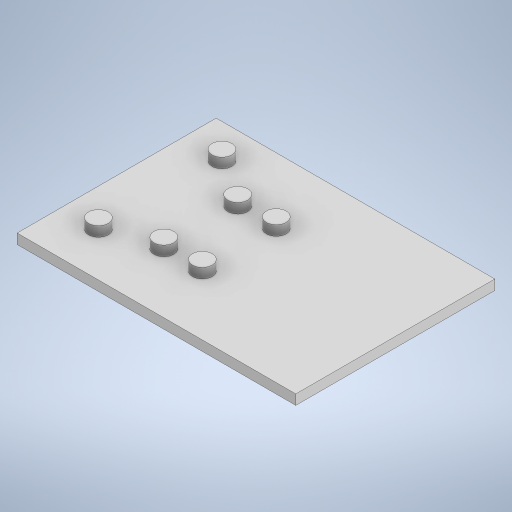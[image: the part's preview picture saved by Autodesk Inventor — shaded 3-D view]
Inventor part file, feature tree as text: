
AUTODESK INVENTOR PART (.ipt)
format: ipt  version: 2024 (Build 280153000, 153)  size: 242,176 bytes
history: native  units: mm
features: extrude x2, sketch x2
ambient origin geometry x8: Origin, YZ Plane, XZ Plane, XY Plane, X Axis, Y Axis, Z Axis, Center Point
bodies: Solid1 (feature_tree)
feature tree (4):
  extrude  "Extrusion1"  Depth=100.0mm
  extrude  "Extrusion2"  Depth=10.0mm
  sketch  "Sketch1"  dims[d0=140.0mm d1=100.0mm]
  sketch  "Sketch2"  dims[d2=5.0mm d3=0.0mm d4=10.0mm d5=10.0mm d6=10.0mm d7=10.0mm d8=10.0mm d9=10.0mm d10=5.0mm d11=0.0mm]
